# Revit family: MixerSet_BathKitchen_Nero_Mecca_Edge
name_source: partatom
category: Plumbing Fixtures
units: mm (PartAtom-declared; Revit-internal decimal feet)

## family parameters
Always vertical = Yes
Cut with Voids When Loaded = Yes
Maintain Annotation Orientation = No
OmniClass Number = 23.31.11.19
OmniClass Title = Faucet Mixing Valves
Part Type = Normal
Room Calculation Point = No
Round Connector Dimension = Use Diameter
Shared = No
Work Plane-Based = No

## types (7) — shared parameters
Assembly Code = D2010
CW Connection = Yes
Default Elevation = 900 mm  [stored 2.95276 ft]
HW Connection = Yes
IfcExportAs = IfcValve
IfcExportType = MIXING
Manufacturer = Nero
ManufacturerOverallDepth = 242.5 mm  [stored 0.795604 ft]
ManufacturerOverallHeight = 270.5 mm  [stored 0.887467 ft]
ManufacturerOverallWidth = 220 mm  [stored 0.721785 ft]
ModifiedIssue = 20251009 $
URL = https://nerotapware.com.au
Uniclass2015Code = Pr_40_20_87
Uniclass2015Title = Taps and water supply outlet fittings
Uniclass2015Version = Products v1.35
Vent Connection = No
Waste Connection = No
zero-valued in all types: CWFU, HWFU, WFU

## per-type parameters (varying)
| type | Description | ManufacturerSpecCode | Material | Model | Type Comments |
| Chrome (NR221901kCH) | Mecca Hob Bath/Kitchen Mixer Set Edge Spout Chrome | NR221901kCH | Metal_Chrome_Nero | NR221901kCH | Mixer Set - Bath Kitchen - Edge - Chrome |
| Matte Black (NR221901kMB) | Mecca Hob Bath/Kitchen Mixer Set Edge Spout Matte Black | NR221901kMB | Metal_MatteBlack_Nero | NR221901kMB | Mixer Set - Bath Kitchen - Edge - Matte Black |
| Brushed Nickel (NR221901kBN) | Mecca Hob Bath/Kitchen Mixer Set Edge Spout Brushed Nickel | NR221901kBN | Metal_Nickel_Nero_Brushed | NR221901kBN | Mixer Set - Bath Kitchen - Edge - Brushed Nickel |
| Gun Metal (NR221901kGM) | Mecca Hob Bath/Kitchen Mixer Set Edge Spout Gun Metal | NR221901kGM | Metal_GunMetal_Nero | NR221901kGM | Mixer Set - Bath Kitchen - Edge - Gun Metal |
| Brushed Gold (NR221901kBG) | Mecca Hob Bath/Kitchen Mixer Set Edge Spout Brushed Gold | NR221901kBG | Metal_Gold_Nero_Brushed | NR221901kBG | Mixer Set - Bath Kitchen - Edge - Brushed Gold |
| Brushed Bronze (NR221901kBZ) | Mecca Hob Bath/Kitchen Mixer Set Edge Spout Brushed Bronze | NR221901kBZ | Metal_Bronze_Nero_Brushed | NR221901kBZ | Mixer Set - Bath Kitchen - Edge - Brushed Bronze |
| Matte White (NR221901kMW) | Mecca Hob Bath/Kitchen Mixer Set Edge Spout Matte White | NR221901kMW | Metal_MatteWhite_Nero | NR221901kMW | Mixer Set - Bath Kitchen - Edge - Matte White |

note: [stored X ft] marks values corroborated as IEEE doubles in the binary element streams (Revit-internal decimal feet)

## geometry (parser evidence)
native form markers: Sweep x3
no freeform markers — native parametric forms only
